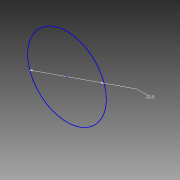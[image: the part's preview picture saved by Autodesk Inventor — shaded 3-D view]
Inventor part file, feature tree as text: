
AUTODESK INVENTOR PART (.ipt)
format: ipt  version: 2012 (Build 160160000, 160)  size: 67,072 bytes
history: native  units: in
note: dims shown in document units (in); Inventor stores cm internally (conversion verified against a paired STEP export)
features: extrude x1, sketch x1
ambient origin geometry x8: Origin, YZ Plane, XZ Plane, XY Plane, X Axis, Y Axis, Z Axis, Center Point
bodies: Solid1 (feature_tree)
feature tree (2):
  extrude  "Extrusion1"  Depth=0.1575in TaperAngle=0.0deg
  sketch  "Sketch1"  dims[d0=0.8858in d1=0.1575in d2=0.0in]
